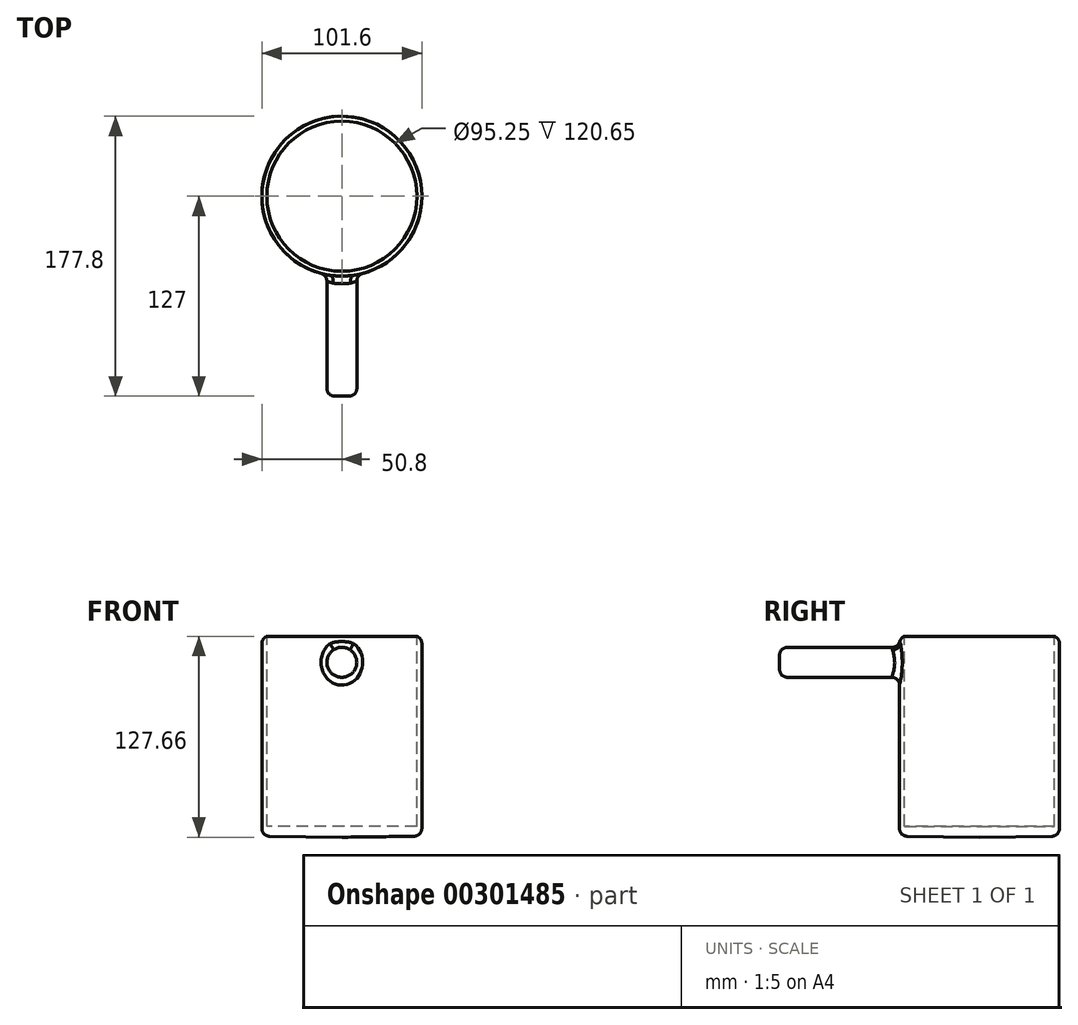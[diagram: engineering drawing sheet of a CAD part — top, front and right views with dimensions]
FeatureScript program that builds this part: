
annotation { "Feature Type Name" : "Feature", "Feature Type Description" : "" }
export const myFeature = defineFeature(function(context is Context, id is Id, definition is map)
    precondition{}
    {
        {
            var Q0;
            Q0=qCreatedBy(makeId("Front.planeOp"),FACE);
            var sketch = newSketch(context, id + "F0", { "sketchPlane" : qUnion([Q0])});
            skLineSegment(sketch, "E0", {"start": v(0, -29.69) * mm, "end": v(0, 97.97) * mm});
            skLineSegment(sketch, "E1", {"start": v(0, 97.97) * mm, "end": v(-50.8, 97.97) * mm});
            skLineSegment(sketch, "E2", {"start": v(-50.8, 97.97) * mm, "end": v(-50.8, -29.03) * mm});
            skLineSegment(sketch, "E3", {"start": v(-50.8, -29.03) * mm, "end": v(0, -29.69) * mm});
            skSolve(sketch);
        }
        {
            var Q0;
            Q0 = qSketchRegion(id + "F0", true);
            var Q1;
            Q1=sQuery(id+"F0.wireOp",EDGE,"E0");
            revolve(context, id + "F1", {"entities" : qUnion([Q0]), "axis" : qUnion([Q1]), "revolveType" : RevolveType.FULL});
        }
        {
            var Q0;
            Q0=makeQuery(id+"F1.opRevolve","SWEPT_FACE",FACE,{"disambiguationData":[OSD([sQuery(id+"F0.wireOp",EDGE,"E1")])]});
            var sketch = newSketch(context, id + "F2", { "sketchPlane" : qUnion([Q0])});
            skCircle(sketch, "E4", {"center": v(0, 0) * mm, "radius": 47.62 * mm});
            skSolve(sketch);
        }
        {
            var Q0;
            Q0=makeQuery(id+"F2.imprint","IMPRINT",FACE,{"disambiguationData":[TD([[makeQuery(id+"F2.imprint","IMPRINT",EDGE,{"derivedFrom":sQuery(id+"F2.wireOp",EDGE,"E4")}),1.0]])]});
            extrude(context, id + "F3", {"entities" : qUnion([Q0]), "operationType" : NewBodyOperationType.REMOVE, "oppositeDirection" : true, "depth" : 120.65 * mm});
        }
        {
            var Q0;
            Q0=makeQuery(id+"F1.opRevolve","SWEPT_EDGE",EDGE,{"disambiguationData":[OSD([sQuery(id+"F0.wireOp",EDGE,"E1"),sQuery(id+"F0.wireOp",EDGE,"E2")])]});
            var Q1;
            Q1=makeQuery(id+"F1.opRevolve","SWEPT_EDGE",EDGE,{"disambiguationData":[OSD([sQuery(id+"F0.wireOp",EDGE,"E2"),sQuery(id+"F0.wireOp",EDGE,"E3")])]});
            fillet(context, id + "F4", {"entities" : qUnion([Q0, Q1]), "radius" : 5 * mm, "tangentPropagation" : true, "allowEdgeOverflow" : false});
        }
        {
            var Q0;
            Q0=qCreatedBy(makeId("Front.planeOp"),FACE);
            var sketch = newSketch(context, id + "F5", { "sketchPlane" : qUnion([Q0])});
            skCircle(sketch, "E5", {"center": v(0, 81.42) * mm, "radius": 9.53 * mm});
            skSolve(sketch);
        }
        {
            var Q0;
            Q0 = qSketchRegion(id + "F5", true);
            extrude(context, id + "F6", {"entities" : qUnion([Q0]), "operationType" : NewBodyOperationType.ADD, "depth" : 127 * mm});
        }
        {
            var Q0;
            Q0=makeQuery(id+"F6.opExtrude","CAP_EDGE",EDGE,{"disambiguationData":[OSD([sQuery(id+"F5.wireOp",EDGE,"E5")])],"isStart":false});
            var Q1;
            Q1=makeQuery(id+"F6.boolean.opBoolean","INTERSECT",EDGE,{"derivedFrom":[makeQuery(id+"F1.opRevolve","SWEPT_FACE",FACE,{"disambiguationData":[OSD([sQuery(id+"F0.wireOp",EDGE,"E2")])]}),makeQuery(id+"F6.opExtrude","SWEPT_FACE",FACE,{"disambiguationData":[OSD([sQuery(id+"F5.wireOp",EDGE,"E5")])]})]});
            fillet(context, id + "F7", {"entities" : qUnion([Q0, Q1]), "radius" : 5 * mm, "tangentPropagation" : true, "allowEdgeOverflow" : false});
        }
        {
            var Q0;
            Q0=makeQuery(id+"F6.opExtrude","CAP_FACE",FACE,{"disambiguationData":[OSD([sQuery(id+"F5.wireOp",EDGE,"E5")])],"isStart":true});
            var Q1;
            Q1=makeQuery(id+"F3.boolean.opBoolean","COPY",FACE,{"derivedFrom":makeQuery(id+"F3.opExtrude","SWEPT_FACE",FACE,{"disambiguationData":[OSD([sQuery(id+"F2.wireOp",EDGE,"E4")])]})});
            extrude(context, id + "F8", {"entities" : qUnion([Q0]), "operationType" : NewBodyOperationType.REMOVE, "endBound" : BoundingType.UP_TO_SURFACE, "oppositeDirection" : true, "endBoundEntityFace" : qUnion([Q1]), "depth" : 25 * mm});
        }
    });
